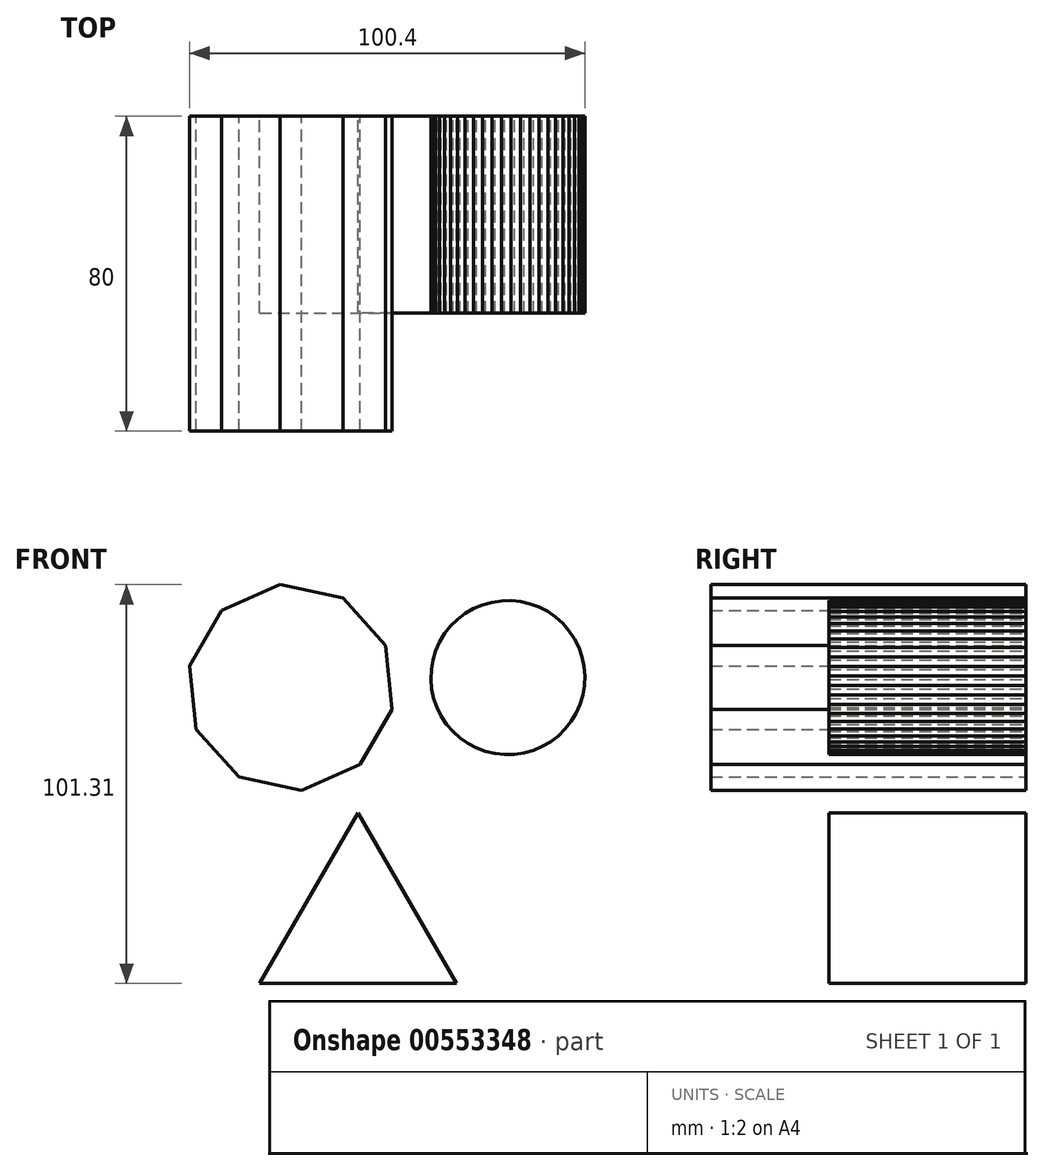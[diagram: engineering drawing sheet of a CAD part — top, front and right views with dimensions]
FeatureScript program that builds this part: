
annotation { "Feature Type Name" : "Feature", "Feature Type Description" : "" }
export const myFeature = defineFeature(function(context is Context, id is Id, definition is map)
    precondition{}
    {
        {
            var Q0;
            Q0=qCreatedBy(makeId("Front.planeOp"),FACE);
            var sketch = newSketch(context, id + "F0", { "sketchPlane" : qUnion([Q0])});
            skLineSegment(sketch, "E0", {"start": v(-50, -28.95) * mm, "end": v(0, -28.95) * mm});
            skLineSegment(sketch, "E1", {"start": v(-50, -28.95) * mm, "end": v(-25, 14.35) * mm});
            skLineSegment(sketch, "E2", {"start": v(0, -28.95) * mm, "end": v(-25, 14.35) * mm});
            skSolve(sketch);
        }
        {
            var Q0;
            Q0 = qSketchRegion(id + "F0", true);
            extrude(context, id + "F1", {"entities" : qUnion([Q0]), "depth" : 50 * mm, "offsetDistance" : 25 * mm});
        }
        {
            var Q0;
            Q0=qCreatedBy(makeId("Front.planeOp"),FACE);
            var sketch = newSketch(context, id + "F2", { "sketchPlane" : qUnion([Q0])});
            skCircle(sketch, "E3.cCircle", {"center": v(-42.12, 46.21) * mm, "radius": 25 * mm, "construction": true});
            skLineSegment(sketch, "E3.0", {"start": v(-16.42, 40.68) * mm, "end": v(-24.57, 26.63) * mm});
            skLineSegment(sketch, "E3.1", {"start": v(-24.57, 26.63) * mm, "end": v(-39.43, 20.06) * mm});
            skLineSegment(sketch, "E3.2", {"start": v(-39.43, 20.06) * mm, "end": v(-55.32, 23.48) * mm});
            skLineSegment(sketch, "E3.3", {"start": v(-55.32, 23.48) * mm, "end": v(-66.16, 35.58) * mm});
            skLineSegment(sketch, "E3.4", {"start": v(-66.16, 35.58) * mm, "end": v(-67.81, 51.74) * mm});
            skLineSegment(sketch, "E3.5", {"start": v(-67.81, 51.74) * mm, "end": v(-59.66, 65.79) * mm});
            skLineSegment(sketch, "E3.6", {"start": v(-59.66, 65.79) * mm, "end": v(-44.8, 72.36) * mm});
            skLineSegment(sketch, "E3.7", {"start": v(-44.8, 72.36) * mm, "end": v(-28.92, 68.94) * mm});
            skLineSegment(sketch, "E3.8", {"start": v(-28.92, 68.94) * mm, "end": v(-18.08, 56.84) * mm});
            skLineSegment(sketch, "E3.9", {"start": v(-18.08, 56.84) * mm, "end": v(-16.42, 40.68) * mm});
            skPoint(sketch, "E3.0.midPoint", {"position": v(-20.5, 33.66) * mm});
            skSolve(sketch);
        }
        {
            var Q0;
            Q0 = qSketchRegion(id + "F2", true);
            extrude(context, id + "F3", {"entities" : qUnion([Q0]), "depth" : 80 * mm, "offsetDistance" : 25 * mm});
        }
        {
            var Q0;
            Q0=qCreatedBy(makeId("Front.planeOp"),FACE);
            var sketch = newSketch(context, id + "F4", { "sketchPlane" : qUnion([Q0])});
            skCircle(sketch, "E4.cCircle", {"center": v(13.03, 48.72) * mm, "radius": 19.53 * mm, "construction": true});
            skLineSegment(sketch, "E4.0", {"start": v(31.38, 41.91) * mm, "end": v(30.38, 39.67) * mm});
            skLineSegment(sketch, "E4.1", {"start": v(30.38, 39.67) * mm, "end": v(29.1, 37.57) * mm});
            skLineSegment(sketch, "E4.2", {"start": v(29.1, 37.57) * mm, "end": v(27.58, 35.64) * mm});
            skLineSegment(sketch, "E4.3", {"start": v(27.58, 35.64) * mm, "end": v(25.83, 33.92) * mm});
            skLineSegment(sketch, "E4.4", {"start": v(25.83, 33.92) * mm, "end": v(23.87, 32.43) * mm});
            skLineSegment(sketch, "E4.5", {"start": v(23.87, 32.43) * mm, "end": v(21.74, 31.2) * mm});
            skLineSegment(sketch, "E4.6", {"start": v(21.74, 31.2) * mm, "end": v(19.48, 30.25) * mm});
            skLineSegment(sketch, "E4.7", {"start": v(19.48, 30.25) * mm, "end": v(17.11, 29.59) * mm});
            skLineSegment(sketch, "E4.8", {"start": v(17.11, 29.59) * mm, "end": v(14.68, 29.22) * mm});
            skLineSegment(sketch, "E4.9", {"start": v(14.68, 29.22) * mm, "end": v(12.22, 29.17) * mm});
            skLineSegment(sketch, "E4.10", {"start": v(12.22, 29.17) * mm, "end": v(9.78, 29.43) * mm});
            skLineSegment(sketch, "E4.11", {"start": v(9.78, 29.43) * mm, "end": v(7.39, 29.99) * mm});
            skLineSegment(sketch, "E4.12", {"start": v(7.39, 29.99) * mm, "end": v(5.08, 30.84) * mm});
            skLineSegment(sketch, "E4.13", {"start": v(5.08, 30.84) * mm, "end": v(2.9, 31.98) * mm});
            skLineSegment(sketch, "E4.14", {"start": v(2.9, 31.98) * mm, "end": v(0.89, 33.38) * mm});
            skLineSegment(sketch, "E4.15", {"start": v(0.89, 33.38) * mm, "end": v(-0.94, 35.02) * mm});
            skLineSegment(sketch, "E4.16", {"start": v(-0.94, 35.02) * mm, "end": v(-2.55, 36.88) * mm});
            skLineSegment(sketch, "E4.17", {"start": v(-2.55, 36.88) * mm, "end": v(-3.9, 38.93) * mm});
            skLineSegment(sketch, "E4.18", {"start": v(-3.9, 38.93) * mm, "end": v(-5, 41.13) * mm});
            skLineSegment(sketch, "E4.19", {"start": v(-5, 41.13) * mm, "end": v(-5.81, 43.45) * mm});
            skLineSegment(sketch, "E4.20", {"start": v(-5.81, 43.45) * mm, "end": v(-6.33, 45.85) * mm});
            skLineSegment(sketch, "E4.21", {"start": v(-6.33, 45.85) * mm, "end": v(-6.53, 48.3) * mm});
            skLineSegment(sketch, "E4.22", {"start": v(-6.53, 48.3) * mm, "end": v(-6.43, 50.76) * mm});
            skLineSegment(sketch, "E4.23", {"start": v(-6.43, 50.76) * mm, "end": v(-6.02, 53.18) * mm});
            skLineSegment(sketch, "E4.24", {"start": v(-6.02, 53.18) * mm, "end": v(-5.31, 55.53) * mm});
            skLineSegment(sketch, "E4.25", {"start": v(-5.31, 55.53) * mm, "end": v(-4.32, 57.78) * mm});
            skLineSegment(sketch, "E4.26", {"start": v(-4.32, 57.78) * mm, "end": v(-3.05, 59.88) * mm});
            skLineSegment(sketch, "E4.27", {"start": v(-3.05, 59.88) * mm, "end": v(-1.52, 61.8) * mm});
            skLineSegment(sketch, "E4.28", {"start": v(-1.52, 61.8) * mm, "end": v(0.23, 63.53) * mm});
            skLineSegment(sketch, "E4.29", {"start": v(0.23, 63.53) * mm, "end": v(2.2, 65.01) * mm});
            skLineSegment(sketch, "E4.30", {"start": v(2.2, 65.01) * mm, "end": v(4.32, 66.24) * mm});
            skLineSegment(sketch, "E4.31", {"start": v(4.32, 66.24) * mm, "end": v(6.58, 67.2) * mm});
            skLineSegment(sketch, "E4.32", {"start": v(6.58, 67.2) * mm, "end": v(8.95, 67.86) * mm});
            skLineSegment(sketch, "E4.33", {"start": v(8.95, 67.86) * mm, "end": v(11.38, 68.22) * mm});
            skLineSegment(sketch, "E4.34", {"start": v(11.38, 68.22) * mm, "end": v(13.84, 68.27) * mm});
            skLineSegment(sketch, "E4.35", {"start": v(13.84, 68.27) * mm, "end": v(16.28, 68.02) * mm});
            skLineSegment(sketch, "E4.36", {"start": v(16.28, 68.02) * mm, "end": v(18.67, 67.46) * mm});
            skLineSegment(sketch, "E4.37", {"start": v(18.67, 67.46) * mm, "end": v(20.98, 66.6) * mm});
            skLineSegment(sketch, "E4.38", {"start": v(20.98, 66.6) * mm, "end": v(23.16, 65.47) * mm});
            skLineSegment(sketch, "E4.39", {"start": v(23.16, 65.47) * mm, "end": v(25.18, 64.07) * mm});
            skLineSegment(sketch, "E4.40", {"start": v(25.18, 64.07) * mm, "end": v(27, 62.42) * mm});
            skLineSegment(sketch, "E4.41", {"start": v(27, 62.42) * mm, "end": v(28.6, 60.56) * mm});
            skLineSegment(sketch, "E4.42", {"start": v(28.6, 60.56) * mm, "end": v(29.97, 58.52) * mm});
            skLineSegment(sketch, "E4.43", {"start": v(29.97, 58.52) * mm, "end": v(31.06, 56.32) * mm});
            skLineSegment(sketch, "E4.44", {"start": v(31.06, 56.32) * mm, "end": v(31.87, 54) * mm});
            skLineSegment(sketch, "E4.45", {"start": v(31.87, 54) * mm, "end": v(32.39, 51.6) * mm});
            skLineSegment(sketch, "E4.46", {"start": v(32.39, 51.6) * mm, "end": v(32.6, 49.15) * mm});
            skLineSegment(sketch, "E4.47", {"start": v(32.6, 49.15) * mm, "end": v(32.5, 46.7) * mm});
            skLineSegment(sketch, "E4.48", {"start": v(32.5, 46.7) * mm, "end": v(32.08, 44.27) * mm});
            skLineSegment(sketch, "E4.49", {"start": v(32.08, 44.27) * mm, "end": v(31.38, 41.91) * mm});
            skPoint(sketch, "E4.0.midPoint", {"position": v(30.88, 40.8) * mm});
            skSolve(sketch);
        }
        {
            var Q0;
            Q0=makeQuery(id+"F4.imprint","IMPRINT",FACE,{"disambiguationData":[TD([[makeQuery(id+"F4.imprint","IMPRINT",EDGE,{"derivedFrom":sQuery(id+"F4.wireOp",EDGE,"E4.0")}),-1.0]])]});
            extrude(context, id + "F5", {"entities" : qUnion([Q0]), "depth" : 50 * mm, "offsetDistance" : 25 * mm});
        }
        {
            var Q0;
            Q0=qCreatedBy(makeId("Front.planeOp"),FACE);
            var sketch = newSketch(context, id + "F6", { "sketchPlane" : qUnion([Q0])});
            skCircle(sketch, "E5", {"center": v(32.58, -15.86) * mm, "radius": 17.18 * mm});
            skSolve(sketch);
        }
        {
            var Q0;
            Q0=sQuery(id+"F6.wireOp",EDGE,"E5");
            extrude(context, id + "F7", {"bodyType" : ToolBodyType.SURFACE, "surfaceEntities" : qUnion([Q0]), "depth" : 96.8 * mm, "offsetDistance" : 25 * mm});
        }
    });
